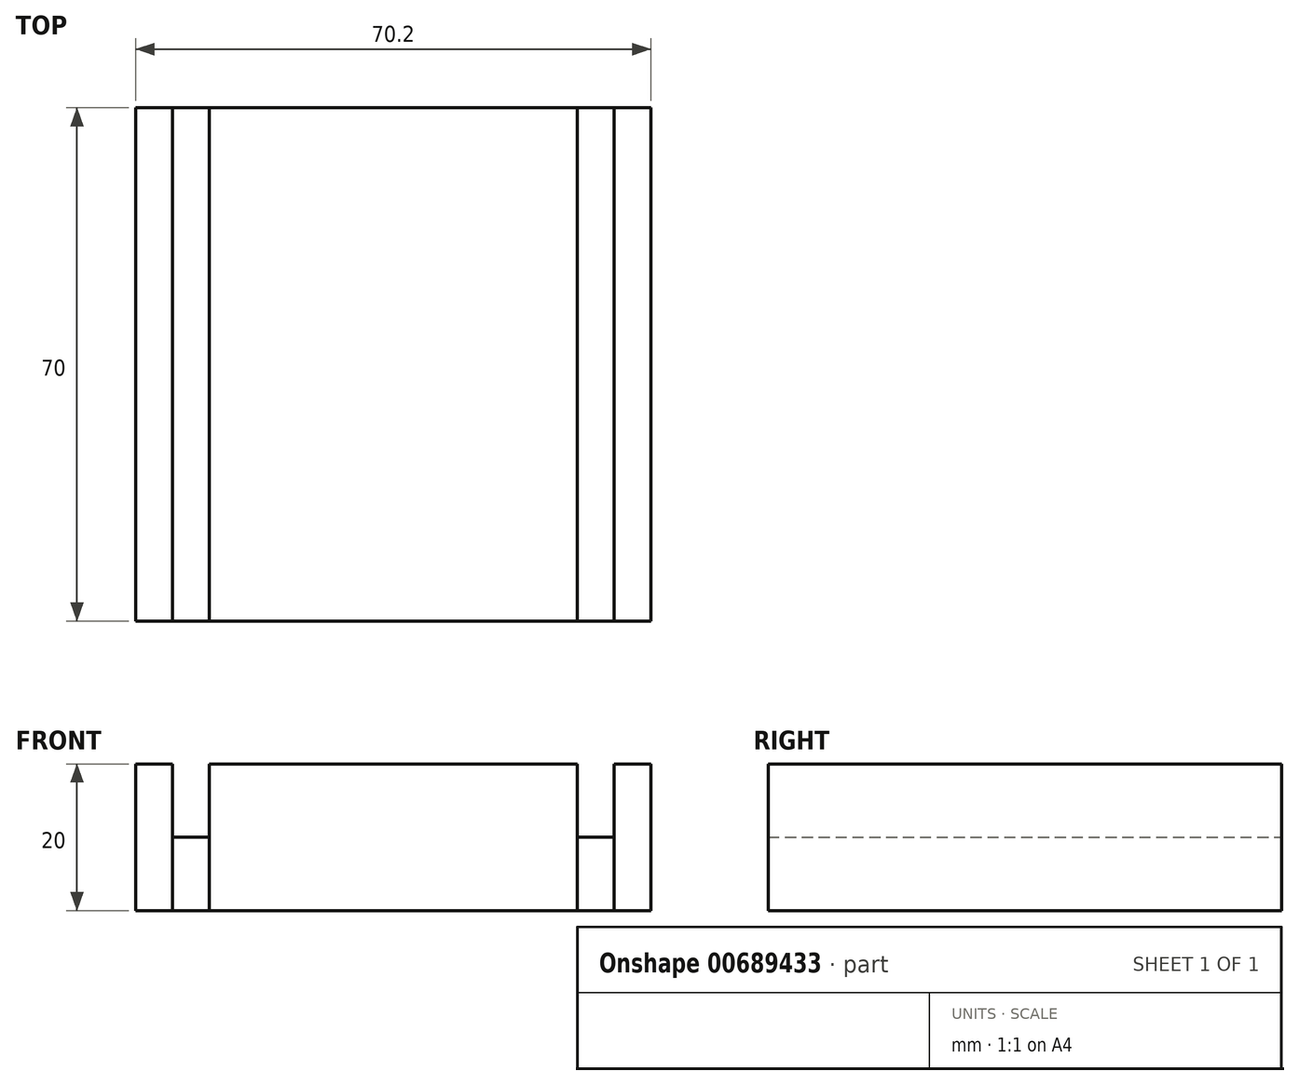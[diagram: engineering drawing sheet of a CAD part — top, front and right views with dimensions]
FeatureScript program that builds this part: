
annotation { "Feature Type Name" : "Feature", "Feature Type Description" : "" }
export const myFeature = defineFeature(function(context is Context, id is Id, definition is map)
    precondition{}
    {
        {
            var Q0;
            Q0=qCreatedBy(makeId("Top.planeOp"),FACE);
            var sketch = newSketch(context, id + "F0", { "sketchPlane" : qUnion([Q0])});
            skLineSegment(sketch, "E0.bottom", {"start": v(-56.4, 36.73) * mm, "end": v(13.8, 36.73) * mm});
            skLineSegment(sketch, "E0.top", {"start": v(-56.4, -33.27) * mm, "end": v(13.8, -33.27) * mm});
            skLineSegment(sketch, "E0.left", {"start": v(-56.4, 36.73) * mm, "end": v(-56.4, -33.27) * mm});
            skLineSegment(sketch, "E0.right", {"start": v(13.8, 36.73) * mm, "end": v(13.8, -33.27) * mm});
            skLineSegment(sketch, "E1", {"start": v(-48.9, 36.73) * mm, "end": v(-48.9, -33.27) * mm});
            skLineSegment(sketch, "E2", {"start": v(6.3, -33.27) * mm, "end": v(6.3, 36.73) * mm});
            skArc(sketch, "E3.0.startCap", {"start": v(-51.4, 36.73) * mm, "mid": v(-48.9, 39.23) * mm, "end": v(-46.4, 36.73) * mm});
            skArc(sketch, "E3.0.endCap", {"start": v(-46.4, -33.27) * mm, "mid": v(-48.9, -35.77) * mm, "end": v(-51.4, -33.27) * mm});
            skLineSegment(sketch, "E3.0.left", {"start": v(-46.4, 36.73) * mm, "end": v(-46.4, -33.27) * mm});
            skLineSegment(sketch, "E3.0.right", {"start": v(-51.4, 36.73) * mm, "end": v(-51.4, -33.27) * mm});
            skArc(sketch, "E3.1.startCap", {"start": v(8.8, -33.27) * mm, "mid": v(6.3, -35.77) * mm, "end": v(3.8, -33.27) * mm});
            skArc(sketch, "E3.1.endCap", {"start": v(3.8, 36.73) * mm, "mid": v(6.3, 39.23) * mm, "end": v(8.8, 36.73) * mm});
            skLineSegment(sketch, "E3.1.left", {"start": v(3.8, -33.27) * mm, "end": v(3.8, 36.73) * mm});
            skLineSegment(sketch, "E3.1.right", {"start": v(8.8, -33.27) * mm, "end": v(8.8, 36.73) * mm});
            skSolve(sketch);
        }
        {
            var Q0;
            {var subQ0=sQuery(id+"F0.wireOp",EDGE,"E0.left");Q0=makeQuery(id+"F0.imprint","IMPRINT",FACE,{"disambiguationData":[TD([[makeQuery(id+"F0.imprint","IMPRINT",EDGE,{"derivedFrom":subQ0}),1.0]])]});}
            var Q1;
            {var subQ0=sQuery(id+"F0.wireOp",EDGE,"E3.0.left");Q1=makeQuery(id+"F0.imprint","IMPRINT",FACE,{"disambiguationData":[TD([[makeQuery(id+"F0.imprint","IMPRINT",EDGE,{"derivedFrom":subQ0}),1.0]])]});}
            var Q2;
            {var subQ0=sQuery(id+"F0.wireOp",EDGE,"E0.right");Q2=makeQuery(id+"F0.imprint","IMPRINT",FACE,{"disambiguationData":[TD([[makeQuery(id+"F0.imprint","IMPRINT",EDGE,{"derivedFrom":subQ0}),-1.0]])]});}
            extrude(context, id + "F1", {"entities" : qUnion([Q0, Q1, Q2]), "depth" : 20 * mm, "offsetDistance" : 25 * mm});
        }
        {
            var Q0;
            {var subQ0=sQuery(id+"F0.wireOp",EDGE,"E1");Q0=makeQuery(id+"F0.imprint","IMPRINT",FACE,{"disambiguationData":[TD([[makeQuery(id+"F0.imprint","IMPRINT",EDGE,{"derivedFrom":subQ0}),1.0]])]});}
            var Q1;
            {var subQ0=sQuery(id+"F0.wireOp",EDGE,"E1");Q1=makeQuery(id+"F0.imprint","IMPRINT",FACE,{"disambiguationData":[TD([[makeQuery(id+"F0.imprint","IMPRINT",EDGE,{"derivedFrom":subQ0}),-1.0]])]});}
            var Q2;
            {var subQ0=sQuery(id+"F0.wireOp",EDGE,"E2");Q2=makeQuery(id+"F0.imprint","IMPRINT",FACE,{"disambiguationData":[TD([[makeQuery(id+"F0.imprint","IMPRINT",EDGE,{"derivedFrom":subQ0}),1.0]])]});}
            var Q3;
            {var subQ0=sQuery(id+"F0.wireOp",EDGE,"E2");Q3=makeQuery(id+"F0.imprint","IMPRINT",FACE,{"disambiguationData":[TD([[makeQuery(id+"F0.imprint","IMPRINT",EDGE,{"derivedFrom":subQ0}),-1.0]])]});}
            extrude(context, id + "F2", {"entities" : qUnion([Q0, Q1, Q2, Q3]), "depth" : 10 * mm, "offsetDistance" : 25 * mm});
        }
    });
